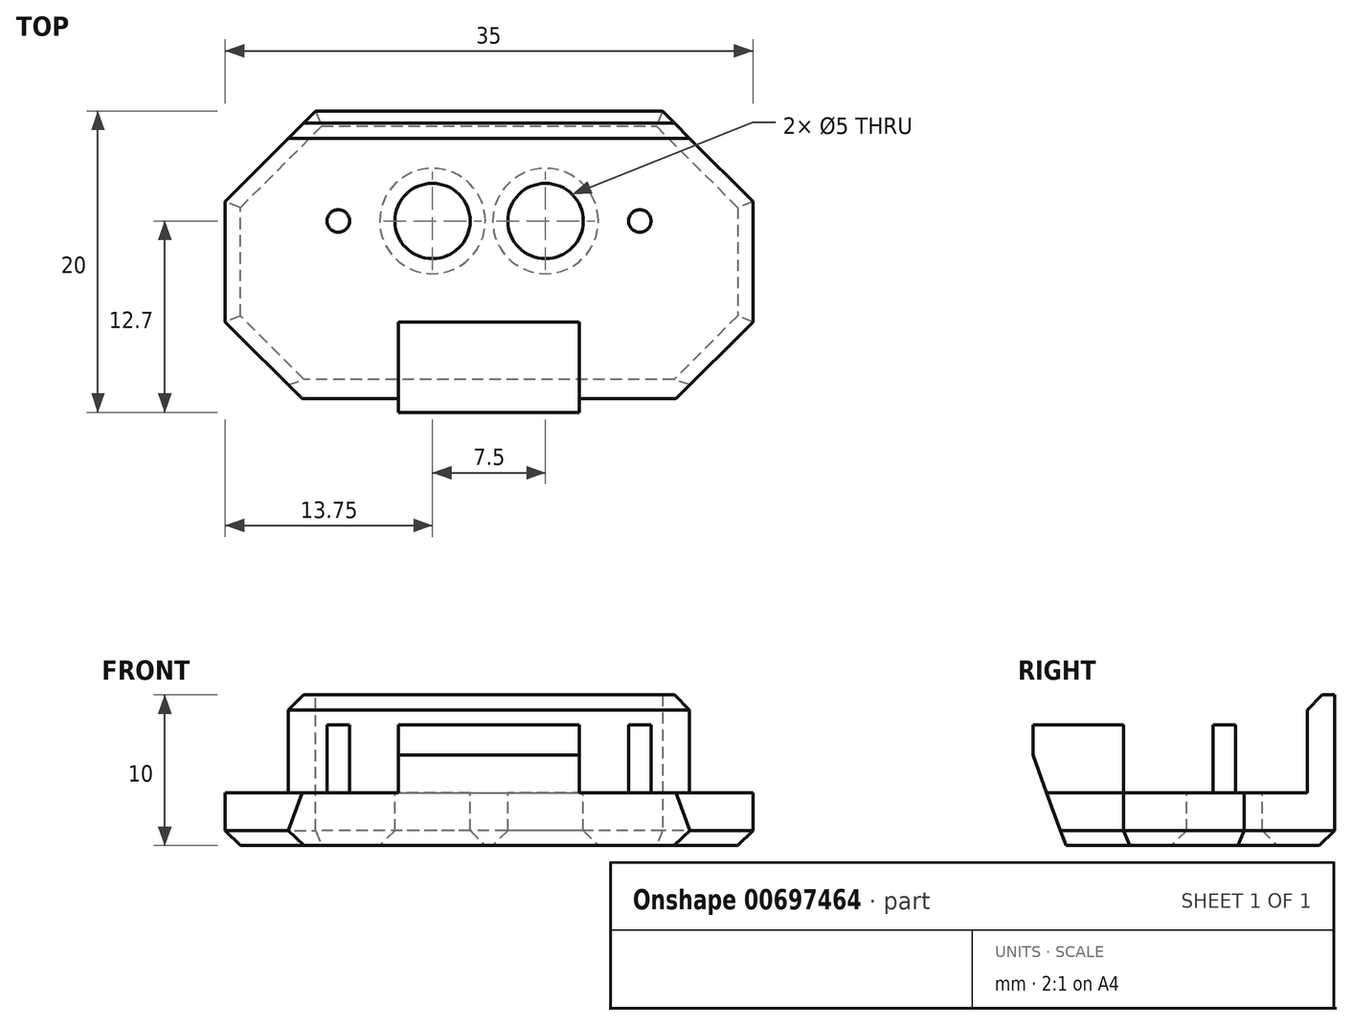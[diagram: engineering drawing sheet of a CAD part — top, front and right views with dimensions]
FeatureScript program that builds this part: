
annotation { "Feature Type Name" : "Feature", "Feature Type Description" : "" }
export const myFeature = defineFeature(function(context is Context, id is Id, definition is map)
    precondition{}
    {
        {
            var Q0;
            Q0=qCreatedBy(makeId("Top.planeOp"),FACE);
            var sketch = newSketch(context, id + "F0", { "sketchPlane" : qUnion([Q0])});
            skLineSegment(sketch, "E0.bottom", {"start": v(0, 0) * mm, "end": v(35, 0) * mm});
            skLineSegment(sketch, "E0.top", {"start": v(0, 20) * mm, "end": v(35, 20) * mm});
            skLineSegment(sketch, "E0.left", {"start": v(0, 0) * mm, "end": v(0, 20) * mm});
            skLineSegment(sketch, "E0.right", {"start": v(35, 0) * mm, "end": v(35, 20) * mm});
            skSolve(sketch);
        }
        {
            var Q0;
            Q0=makeQuery(id+"F0.imprint","IMPRINT",FACE,{"disambiguationData":[TD([[makeQuery(id+"F0.imprint","IMPRINT",EDGE,{"derivedFrom":sQuery(id+"F0.wireOp",EDGE,"E0.bottom")}),1.0]])]});
            extrude(context, id + "F1", {"entities" : qUnion([Q0]), "depth" : 10 * mm, "offsetDistance" : 25 * mm});
        }
        {
            var Q0;
            Q0=makeQuery(id+"F1.opExtrude","CAP_FACE",FACE,{"disambiguationData":[OSD([sQuery(id+"F0.wireOp",EDGE,"E0.bottom"),sQuery(id+"F0.wireOp",EDGE,"E0.top"),sQuery(id+"F0.wireOp",EDGE,"E0.left"),sQuery(id+"F0.wireOp",EDGE,"E0.right")])],"isStart":false});
            var sketch = newSketch(context, id + "F2", { "sketchPlane" : qUnion([Q0])});
            skLineSegment(sketch, "E1.bottom", {"start": v(0, 20) * mm, "end": v(35, 20) * mm});
            skLineSegment(sketch, "E1.top", {"start": v(0, 18.2) * mm, "end": v(35, 18.2) * mm});
            skLineSegment(sketch, "E1.left", {"start": v(0, 20) * mm, "end": v(0, 18.2) * mm});
            skLineSegment(sketch, "E1.right", {"start": v(35, 20) * mm, "end": v(35, 18.2) * mm});
            skCircle(sketch, "E2", {"center": v(7.5, 12.7) * mm, "radius": 0.75 * mm});
            skCircle(sketch, "E3.1.0.0", {"center": v(27.5, 12.7) * mm, "radius": 0.75 * mm});
            skLineSegment(sketch, "E3.direction1", {"start": v(7.5, 12.7) * mm, "end": v(27.5, 12.7) * mm, "construction": true});
            skLineSegment(sketch, "E4.bottom", {"start": v(11.5, 6) * mm, "end": v(23.5, 6) * mm});
            skLineSegment(sketch, "E4.top", {"start": v(11.5, 0) * mm, "end": v(23.5, 0) * mm});
            skLineSegment(sketch, "E4.left", {"start": v(11.5, 6) * mm, "end": v(11.5, 0) * mm});
            skLineSegment(sketch, "E4.right", {"start": v(23.5, 6) * mm, "end": v(23.5, 0) * mm});
            skCircle(sketch, "E5", {"center": v(13.75, 12.7) * mm, "radius": 2.5 * mm});
            skCircle(sketch, "E6.1.0.0", {"center": v(21.25, 12.7) * mm, "radius": 2.5 * mm});
            skLineSegment(sketch, "E6.direction1", {"start": v(13.75, 12.7) * mm, "end": v(21.25, 12.7) * mm, "construction": true});
            skSolve(sketch);
        }
        {
            var Q0;
            {var subQ0=sQuery(id+"F2.wireOp",EDGE,"E1.top");Q0=makeQuery(id+"F2.imprint","IMPRINT",FACE,{"disambiguationData":[TD([[makeQuery(id+"F2.imprint","IMPRINT",EDGE,{"derivedFrom":subQ0}),-1.0]])]});}
            extrude(context, id + "F3", {"entities" : qUnion([Q0]), "operationType" : NewBodyOperationType.REMOVE, "oppositeDirection" : true, "depth" : 6.5 * mm, "offsetDistance" : 25 * mm});
        }
        {
            var Q0;
            Q0=makeQuery(id+"F3.boolean.opBoolean","SPLIT",FACE,{"disambiguationData":[TD([makeQuery(id+"F3.opExtrude","SWEPT_FACE",FACE,{"disambiguationData":[OSD([sQuery(id+"F2.wireOp",EDGE,"E2")])]})])],"derivedFrom":makeQuery(id+"F1.opExtrude","CAP_FACE",FACE,{"disambiguationData":[OSD([sQuery(id+"F0.wireOp",EDGE,"E0.bottom"),sQuery(id+"F0.wireOp",EDGE,"E0.top"),sQuery(id+"F0.wireOp",EDGE,"E0.left"),sQuery(id+"F0.wireOp",EDGE,"E0.right")])],"isStart":false})});
            var Q1;
            {var subQ0=sQuery(id+"F0.wireOp",EDGE,"E0.bottom");Q1=makeQuery(id+"F3.boolean.opBoolean","SPLIT",FACE,{"disambiguationData":[TD([makeQuery(id+"F1.opExtrude","SWEPT_FACE",FACE,{"disambiguationData":[OSD([subQ0])]})])],"derivedFrom":makeQuery(id+"F1.opExtrude","CAP_FACE",FACE,{"disambiguationData":[OSD([subQ0,sQuery(id+"F0.wireOp",EDGE,"E0.top"),sQuery(id+"F0.wireOp",EDGE,"E0.left"),sQuery(id+"F0.wireOp",EDGE,"E0.right")])],"isStart":false})});}
            var Q2;
            Q2=makeQuery(id+"F3.boolean.opBoolean","SPLIT",FACE,{"disambiguationData":[TD([makeQuery(id+"F3.opExtrude","SWEPT_FACE",FACE,{"disambiguationData":[OSD([sQuery(id+"F2.wireOp",EDGE,"E3.1.0.0")])]})])],"derivedFrom":makeQuery(id+"F1.opExtrude","CAP_FACE",FACE,{"disambiguationData":[OSD([sQuery(id+"F0.wireOp",EDGE,"E0.bottom"),sQuery(id+"F0.wireOp",EDGE,"E0.top"),sQuery(id+"F0.wireOp",EDGE,"E0.left"),sQuery(id+"F0.wireOp",EDGE,"E0.right")])],"isStart":false})});
            extrude(context, id + "F4", {"entities" : qUnion([Q0, Q1, Q2]), "operationType" : NewBodyOperationType.REMOVE, "oppositeDirection" : true, "depth" : 2 * mm, "offsetDistance" : 25 * mm});
        }
        {
            var Q0;
            Q0=makeQuery(id+"F3.boolean.opBoolean","SPLIT",FACE,{"disambiguationData":[TD([makeQuery(id+"F3.opExtrude","SWEPT_FACE",FACE,{"disambiguationData":[OSD([sQuery(id+"F2.wireOp",EDGE,"E5")])]})])],"derivedFrom":makeQuery(id+"F1.opExtrude","CAP_FACE",FACE,{"disambiguationData":[OSD([sQuery(id+"F0.wireOp",EDGE,"E0.bottom"),sQuery(id+"F0.wireOp",EDGE,"E0.top"),sQuery(id+"F0.wireOp",EDGE,"E0.left"),sQuery(id+"F0.wireOp",EDGE,"E0.right")])],"isStart":false})});
            var Q1;
            Q1=makeQuery(id+"F3.boolean.opBoolean","SPLIT",FACE,{"disambiguationData":[TD([makeQuery(id+"F3.opExtrude","SWEPT_FACE",FACE,{"disambiguationData":[OSD([sQuery(id+"F2.wireOp",EDGE,"E6.1.0.0")])]})])],"derivedFrom":makeQuery(id+"F1.opExtrude","CAP_FACE",FACE,{"disambiguationData":[OSD([sQuery(id+"F0.wireOp",EDGE,"E0.bottom"),sQuery(id+"F0.wireOp",EDGE,"E0.top"),sQuery(id+"F0.wireOp",EDGE,"E0.left"),sQuery(id+"F0.wireOp",EDGE,"E0.right")])],"isStart":false})});
            extrude(context, id + "F5", {"entities" : qUnion([Q0, Q1]), "operationType" : NewBodyOperationType.REMOVE, "oppositeDirection" : true, "depth" : 25 * mm, "offsetDistance" : 25 * mm});
        }
        {
            var Q0;
            Q0=makeQuery(id+"F1.opExtrude","SWEPT_EDGE",EDGE,{"disambiguationData":[OSD([sQuery(id+"F0.wireOp",EDGE,"E0.bottom"),sQuery(id+"F0.wireOp",EDGE,"E0.right")])]});
            var Q1;
            Q1=makeQuery(id+"F1.opExtrude","SWEPT_EDGE",EDGE,{"disambiguationData":[OSD([sQuery(id+"F0.wireOp",EDGE,"E0.top"),sQuery(id+"F0.wireOp",EDGE,"E0.right")])]});
            var Q2;
            Q2=makeQuery(id+"F1.opExtrude","SWEPT_EDGE",EDGE,{"disambiguationData":[OSD([sQuery(id+"F0.wireOp",EDGE,"E0.bottom"),sQuery(id+"F0.wireOp",EDGE,"E0.left")])]});
            var Q3;
            Q3=makeQuery(id+"F1.opExtrude","SWEPT_EDGE",EDGE,{"disambiguationData":[OSD([sQuery(id+"F0.wireOp",EDGE,"E0.top"),sQuery(id+"F0.wireOp",EDGE,"E0.left")])]});
            chamfer(context, id + "F6", {"entities" : qUnion([Q0, Q1, Q2, Q3]), "chamferType" : ChamferType.OFFSET_ANGLE, "width" : 6 * mm, "oppositeDirection" : false, "angle" : 45 * degree, "tangentPropagation" : true});
        }
        {
            var Q0;
            Q0=makeQuery(id+"F1.opExtrude","CAP_EDGE",EDGE,{"disambiguationData":[OSD([sQuery(id+"F0.wireOp",EDGE,"E0.top")])],"isStart":true});
            var Q1;
            {var subQ0=sQuery(id+"F0.wireOp",EDGE,"E0.right");var subQ1=sQuery(id+"F0.wireOp",EDGE,"E0.top");Q1=makeQuery(id+"F6.opChamfer","BLEND_EDGE",EDGE,{"blendedFrom":[makeQuery(id+"F1.opExtrude","SWEPT_EDGE",EDGE,{"disambiguationData":[OSD([subQ1,subQ0])]}),makeQuery(id+"F1.opExtrude","CAP_FACE",FACE,{"disambiguationData":[OSD([sQuery(id+"F0.wireOp",EDGE,"E0.bottom"),subQ1,sQuery(id+"F0.wireOp",EDGE,"E0.left"),subQ0])],"isStart":true})],"blendedInto":[makeQuery(id+"F1.opExtrude","CAP_FACE",FACE,{"disambiguationData":[OSD([sQuery(id+"F0.wireOp",EDGE,"E0.bottom"),subQ1,sQuery(id+"F0.wireOp",EDGE,"E0.left"),subQ0])],"isStart":true})]});}
            var Q2;
            {var subQ0=sQuery(id+"F0.wireOp",EDGE,"E0.left");var subQ1=sQuery(id+"F0.wireOp",EDGE,"E0.top");Q2=makeQuery(id+"F6.opChamfer","BLEND_EDGE",EDGE,{"blendedFrom":[makeQuery(id+"F1.opExtrude","SWEPT_EDGE",EDGE,{"disambiguationData":[OSD([subQ1,subQ0])]}),makeQuery(id+"F1.opExtrude","CAP_FACE",FACE,{"disambiguationData":[OSD([sQuery(id+"F0.wireOp",EDGE,"E0.bottom"),subQ1,subQ0,sQuery(id+"F0.wireOp",EDGE,"E0.right")])],"isStart":true})],"blendedInto":[makeQuery(id+"F1.opExtrude","CAP_FACE",FACE,{"disambiguationData":[OSD([sQuery(id+"F0.wireOp",EDGE,"E0.bottom"),subQ1,subQ0,sQuery(id+"F0.wireOp",EDGE,"E0.right")])],"isStart":true})]});}
            var Q3;
            Q3=makeQuery(id+"F3.boolean.opBoolean","COPY",EDGE,{"derivedFrom":makeQuery(id+"F3.opExtrude","CAP_EDGE",EDGE,{"disambiguationData":[OSD([sQuery(id+"F2.wireOp",EDGE,"E1.top")])],"isStart":true})});
            var Q4;
            Q4=makeQuery(id+"F4.boolean.opBoolean","COPY",EDGE,{"derivedFrom":makeQuery(id+"F4.opExtrude","CAP_EDGE",EDGE,{"disambiguationData":[OSD([sQuery(id+"F2.wireOp",EDGE,"E4.bottom")])],"isStart":false})});
            var Q5;
            Q5=makeQuery(id+"F4.boolean.opBoolean","COPY",EDGE,{"derivedFrom":makeQuery(id+"F4.opExtrude","CAP_EDGE",EDGE,{"disambiguationData":[OSD([sQuery(id+"F2.wireOp",EDGE,"E4.right")])],"isStart":false})});
            var Q6;
            Q6=makeQuery(id+"F4.boolean.opBoolean","COPY",EDGE,{"derivedFrom":makeQuery(id+"F4.opExtrude","CAP_EDGE",EDGE,{"disambiguationData":[OSD([sQuery(id+"F2.wireOp",EDGE,"E4.left")])],"isStart":false})});
            var Q7;
            Q7=makeQuery(id+"F1.opExtrude","CAP_EDGE",EDGE,{"disambiguationData":[OSD([sQuery(id+"F0.wireOp",EDGE,"E0.right")])],"isStart":true});
            var Q8;
            Q8=makeQuery(id+"F1.opExtrude","CAP_EDGE",EDGE,{"disambiguationData":[OSD([sQuery(id+"F0.wireOp",EDGE,"E0.left")])],"isStart":true});
            var Q9;
            Q9=makeQuery(id+"F5.boolean.opBoolean","INTERSECT",EDGE,{"derivedFrom":[makeQuery(id+"F1.opExtrude","CAP_FACE",FACE,{"disambiguationData":[OSD([sQuery(id+"F0.wireOp",EDGE,"E0.bottom"),sQuery(id+"F0.wireOp",EDGE,"E0.top"),sQuery(id+"F0.wireOp",EDGE,"E0.left"),sQuery(id+"F0.wireOp",EDGE,"E0.right")])],"isStart":true}),makeQuery(id+"F5.opExtrude","SWEPT_FACE",FACE,{"disambiguationData":[OSD([sQuery(id+"F2.wireOp",EDGE,"E6.1.0.0")])]})]});
            var Q10;
            Q10=makeQuery(id+"F5.boolean.opBoolean","INTERSECT",EDGE,{"derivedFrom":[makeQuery(id+"F1.opExtrude","CAP_FACE",FACE,{"disambiguationData":[OSD([sQuery(id+"F0.wireOp",EDGE,"E0.bottom"),sQuery(id+"F0.wireOp",EDGE,"E0.top"),sQuery(id+"F0.wireOp",EDGE,"E0.left"),sQuery(id+"F0.wireOp",EDGE,"E0.right")])],"isStart":true}),makeQuery(id+"F5.opExtrude","SWEPT_FACE",FACE,{"disambiguationData":[OSD([sQuery(id+"F2.wireOp",EDGE,"E5")])]})]});
            var Q11;
            {var subQ0=sQuery(id+"F0.wireOp",EDGE,"E0.left");var subQ1=sQuery(id+"F0.wireOp",EDGE,"E0.bottom");Q11=makeQuery(id+"F6.opChamfer","BLEND_EDGE",EDGE,{"blendedFrom":[makeQuery(id+"F1.opExtrude","SWEPT_EDGE",EDGE,{"disambiguationData":[OSD([subQ1,subQ0])]}),makeQuery(id+"F1.opExtrude","CAP_FACE",FACE,{"disambiguationData":[OSD([subQ1,sQuery(id+"F0.wireOp",EDGE,"E0.top"),subQ0,sQuery(id+"F0.wireOp",EDGE,"E0.right")])],"isStart":true})],"blendedInto":[makeQuery(id+"F1.opExtrude","CAP_FACE",FACE,{"disambiguationData":[OSD([subQ1,sQuery(id+"F0.wireOp",EDGE,"E0.top"),subQ0,sQuery(id+"F0.wireOp",EDGE,"E0.right")])],"isStart":true})]});}
            var Q12;
            {var subQ0=sQuery(id+"F0.wireOp",EDGE,"E0.right");var subQ1=sQuery(id+"F0.wireOp",EDGE,"E0.bottom");Q12=makeQuery(id+"F6.opChamfer","BLEND_EDGE",EDGE,{"blendedFrom":[makeQuery(id+"F1.opExtrude","SWEPT_EDGE",EDGE,{"disambiguationData":[OSD([subQ1,subQ0])]}),makeQuery(id+"F1.opExtrude","CAP_FACE",FACE,{"disambiguationData":[OSD([subQ1,sQuery(id+"F0.wireOp",EDGE,"E0.top"),sQuery(id+"F0.wireOp",EDGE,"E0.left"),subQ0])],"isStart":true})],"blendedInto":[makeQuery(id+"F1.opExtrude","CAP_FACE",FACE,{"disambiguationData":[OSD([subQ1,sQuery(id+"F0.wireOp",EDGE,"E0.top"),sQuery(id+"F0.wireOp",EDGE,"E0.left"),subQ0])],"isStart":true})]});}
            chamfer(context, id + "F7", {"entities" : qUnion([Q0, Q1, Q2, Q3, Q4, Q5, Q6, Q7, Q8, Q9, Q10, Q11, Q12]), "width" : 1 * mm, "tangentPropagation" : true});
        }
        {
            var Q0;
            Q0=makeQuery(id+"F1.opExtrude","CAP_EDGE",EDGE,{"disambiguationData":[OSD([sQuery(id+"F0.wireOp",EDGE,"E0.bottom")])],"isStart":true});
            chamfer(context, id + "F8", {"entities" : qUnion([Q0]), "chamferType" : ChamferType.OFFSET_ANGLE, "width" : 6 * mm, "oppositeDirection" : false, "angle" : 20 * degree, "tangentPropagation" : true});
        }
    });
